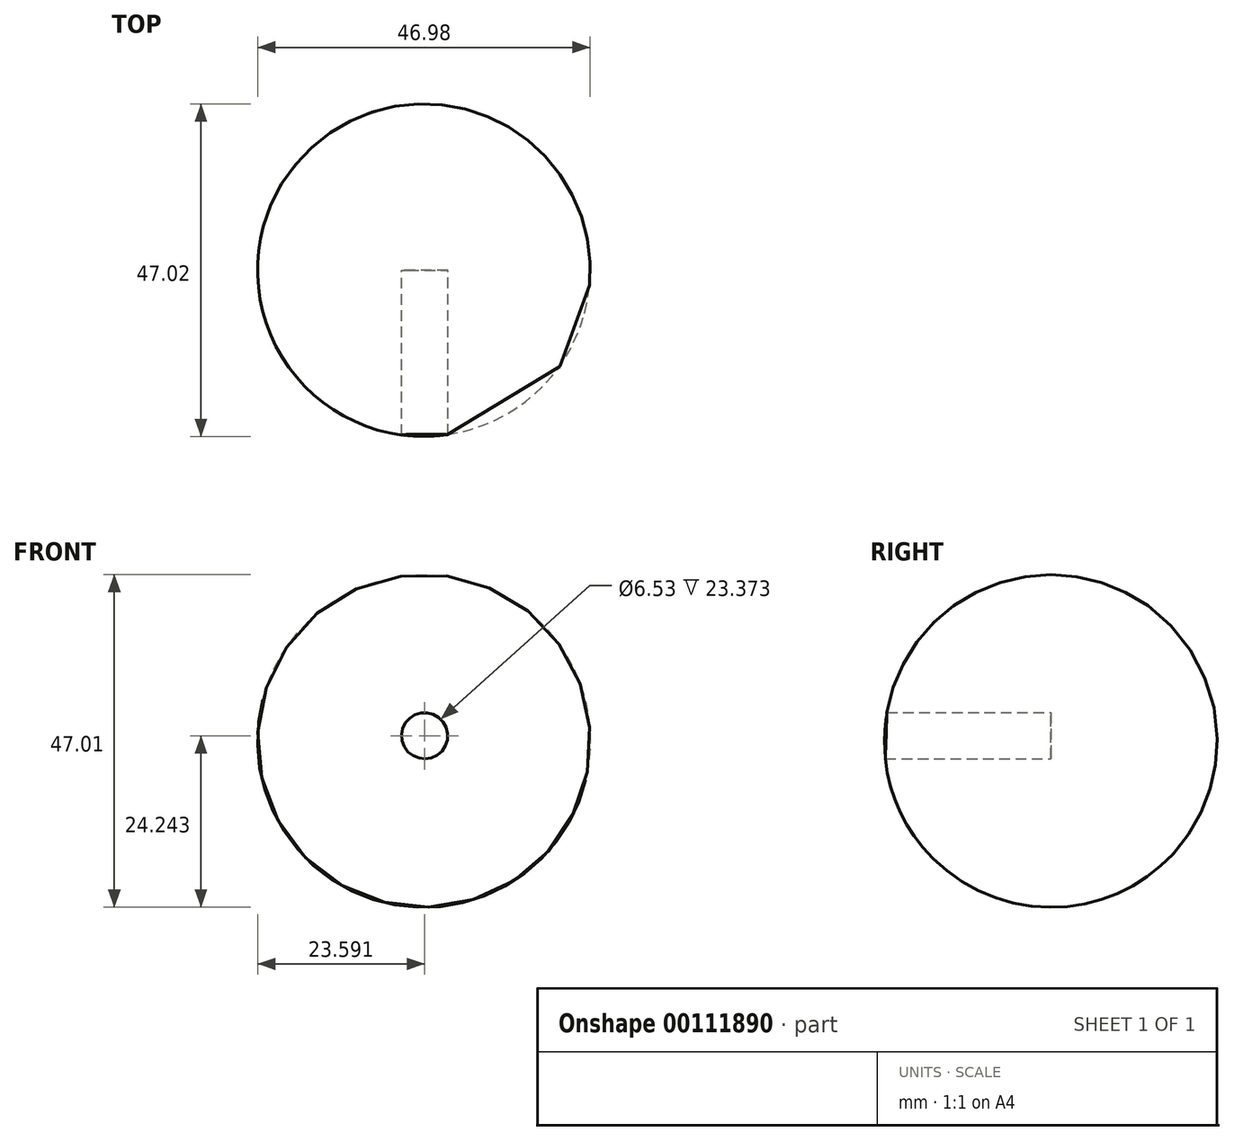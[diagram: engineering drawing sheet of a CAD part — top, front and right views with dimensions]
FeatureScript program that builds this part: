
annotation { "Feature Type Name" : "Feature", "Feature Type Description" : "" }
export const myFeature = defineFeature(function(context is Context, id is Id, definition is map)
    precondition{}
    {
        {
            var Q0;
            Q0=qCreatedBy(makeId("Front.planeOp"),FACE);
            var sketch = newSketch(context, id + "F0", { "sketchPlane" : qUnion([Q0])});
            skArc(sketch, "E0", {"start": v(-31.2, 64.07) * mm, "mid": v(-41.65, 66.04) * mm, "end": v(-42.67, 55.45) * mm});
            skArc(sketch, "E1", {"start": v(-20.63, 56.3) * mm, "mid": v(-20.45, 67.61) * mm, "end": v(-31.2, 64.07) * mm});
            skLineSegment(sketch, "E2", {"start": v(-20.63, 56.3) * mm, "end": v(-31.2, 49.02) * mm});
            skLineSegment(sketch, "E3", {"start": v(-31.2, 49.02) * mm, "end": v(-42.67, 55.45) * mm});
            skSolve(sketch);
        }
        {
            var Q0;
            Q0 = qSketchRegion(id + "F0", true);
            extrude(context, id + "F1", {"entities" : qUnion([Q0]), "depth" : 6.35 * mm});
        }
        {
            var Q0;
            Q0=makeQuery(id+"F1.opExtrude","CAP_EDGE",EDGE,{"disambiguationData":[OSD([sQuery(id+"F0.wireOp",EDGE,"E1")])],"isStart":false});
            var Q1;
            Q1=makeQuery(id+"F1.opExtrude","CAP_EDGE",EDGE,{"disambiguationData":[OSD([sQuery(id+"F0.wireOp",EDGE,"E0")])],"isStart":false});
            var Q2;
            Q2=makeQuery(id+"F1.opExtrude","CAP_EDGE",EDGE,{"disambiguationData":[OSD([sQuery(id+"F0.wireOp",EDGE,"E2")])],"isStart":false});
            var Q3;
            Q3=makeQuery(id+"F1.opExtrude","CAP_EDGE",EDGE,{"disambiguationData":[OSD([sQuery(id+"F0.wireOp",EDGE,"E3")])],"isStart":false});
            var Q4;
            Q4=makeQuery(id+"F1.opExtrude","SWEPT_EDGE",EDGE,{"disambiguationData":[OSD([sQuery(id+"F0.wireOp",EDGE,"E0"),sQuery(id+"F0.wireOp",EDGE,"E3")])]});
            var Q5;
            Q5=makeQuery(id+"F1.opExtrude","SWEPT_EDGE",EDGE,{"disambiguationData":[OSD([sQuery(id+"F0.wireOp",EDGE,"E2"),sQuery(id+"F0.wireOp",EDGE,"E3")])]});
            var Q6;
            Q6=makeQuery(id+"F1.opExtrude","CAP_EDGE",EDGE,{"disambiguationData":[OSD([sQuery(id+"F0.wireOp",EDGE,"E3")])],"isStart":true});
            var Q7;
            Q7=makeQuery(id+"F1.opExtrude","CAP_EDGE",EDGE,{"disambiguationData":[OSD([sQuery(id+"F0.wireOp",EDGE,"E0")])],"isStart":true});
            var Q8;
            Q8=makeQuery(id+"F1.opExtrude","CAP_EDGE",EDGE,{"disambiguationData":[OSD([sQuery(id+"F0.wireOp",EDGE,"E1")])],"isStart":true});
            var Q9;
            Q9=makeQuery(id+"F1.opExtrude","SWEPT_EDGE",EDGE,{"disambiguationData":[OSD([sQuery(id+"F0.wireOp",EDGE,"E1"),sQuery(id+"F0.wireOp",EDGE,"E2")])]});
            var Q10;
            Q10=makeQuery(id+"F1.opExtrude","CAP_EDGE",EDGE,{"disambiguationData":[OSD([sQuery(id+"F0.wireOp",EDGE,"E2")])],"isStart":true});
            fillet(context, id + "F2", {"entities" : qUnion([Q0, Q1, Q2, Q3, Q4, Q5, Q6, Q7, Q8, Q9, Q10]), "radius" : 0.5 * mm, "tangentPropagation" : true, "allowEdgeOverflow" : false});
        }
        {
            var Q0;
            Q0=makeQuery(id+"F1.opExtrude","SWEPT_BODY",BODY,{"disambiguationData":[OSD([sQuery(id+"F0.wireOp",EDGE,"E0"),sQuery(id+"F0.wireOp",EDGE,"E1"),sQuery(id+"F0.wireOp",EDGE,"E2"),sQuery(id+"F0.wireOp",EDGE,"E3")])]});
            deleteBodies(context, id + "F3", {"entities" : qUnion([Q0])});
        }
        {
            var Q0;
            Q0=qCreatedBy(makeId("Front.planeOp"),FACE);
            var sketch = newSketch(context, id + "F4", { "sketchPlane" : qUnion([Q0])});
            skArc(sketch, "E4", {"start": v(15.98, 0) * mm, "mid": v(-1.13, 28.48) * mm, "end": v(-29.6, 11.35) * mm});
            skLineSegment(sketch, "E5", {"start": v(-29.6, 11.35) * mm, "end": v(15.98, 0) * mm});
            skSolve(sketch);
        }
        {
            var Q0;
            Q0=makeQuery(id+"F4.imprint","IMPRINT",FACE,{"disambiguationData":[TD([[makeQuery(id+"F4.imprint","IMPRINT",EDGE,{"derivedFrom":sQuery(id+"F4.wireOp",EDGE,"E4")}),1.0]])]});
            var Q1;
            Q1=sQuery(id+"F4.wireOp",EDGE,"E5");
            revolve(context, id + "F5", {"entities" : qUnion([Q0]), "axis" : qUnion([Q1]), "revolveType" : RevolveType.FULL});
        }
        {
            var Q0;
            Q0=qCreatedBy(makeId("Front.planeOp"),FACE);
            var sketch = newSketch(context, id + "F6", { "sketchPlane" : qUnion([Q0])});
            skCircle(sketch, "E6", {"center": v(-6.7, 6.41) * mm, "radius": 3.27 * mm});
            skSolve(sketch);
        }
        {
            var Q0;
            Q0=makeQuery(id+"F6.imprint","IMPRINT",FACE,{"disambiguationData":[TD([[makeQuery(id+"F6.imprint","IMPRINT",EDGE,{"derivedFrom":sQuery(id+"F6.wireOp",EDGE,"E6")}),1.0]])]});
            extrude(context, id + "F7", {"entities" : qUnion([Q0]), "operationType" : NewBodyOperationType.REMOVE, "depth" : 63.5 * mm});
        }
    });
